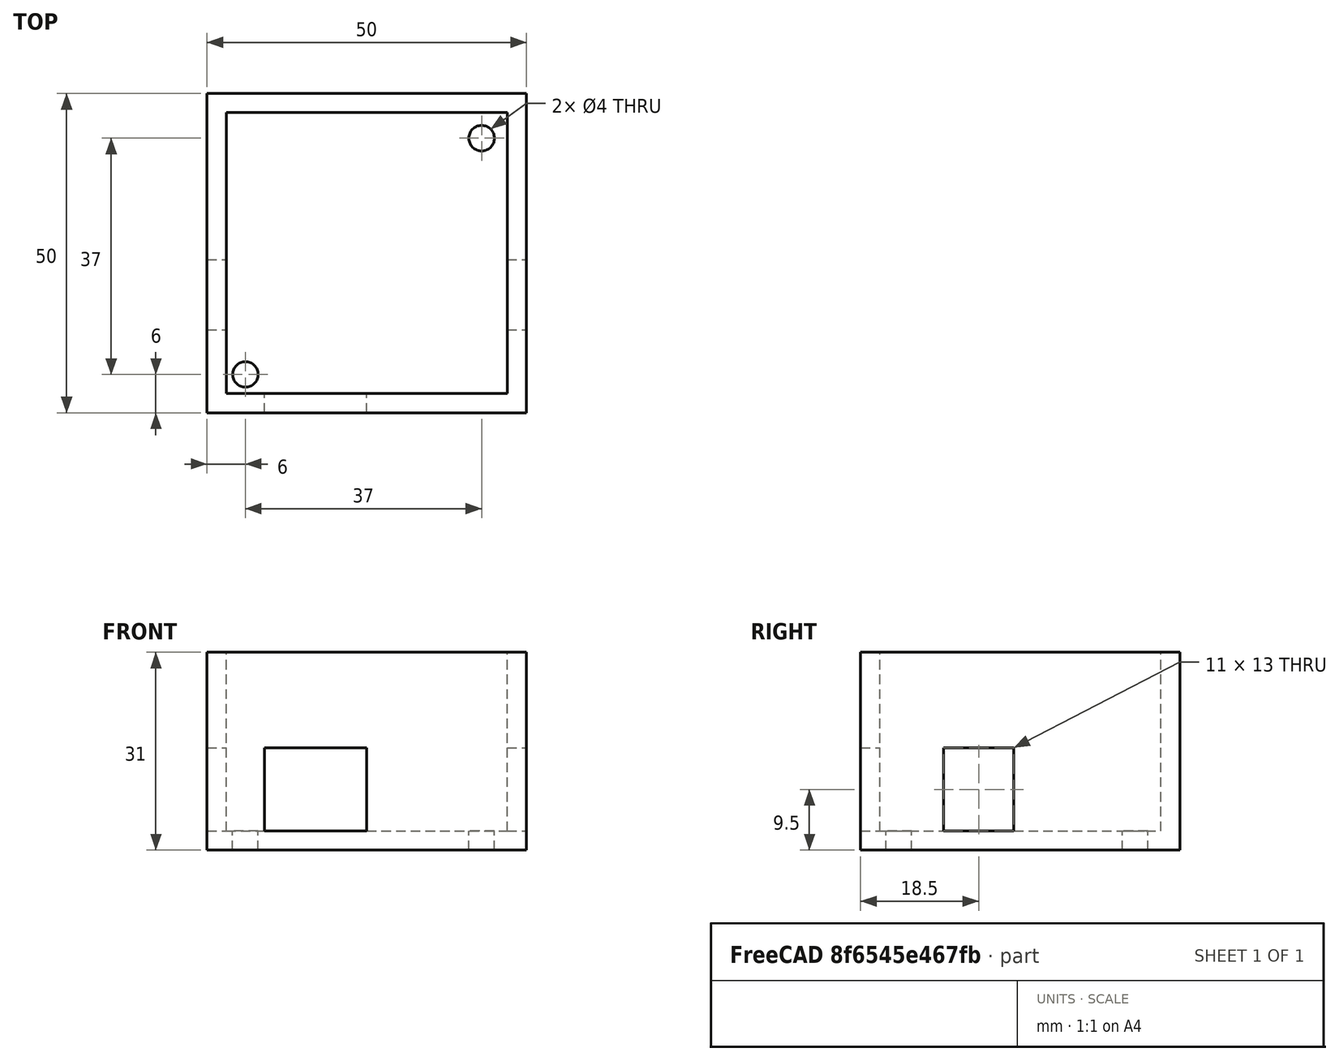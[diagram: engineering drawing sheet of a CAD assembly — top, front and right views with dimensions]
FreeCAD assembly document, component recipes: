
FREECAD ASSEMBLY — COMPONENT RECIPES ("caja_controlador_ruedas")

This assembly document has 2 components, labeled P0..P1 below (a component is one placed body or linked part). 0 of them carry a construction recipe — the FreeCAD feature program that regenerates the part from scratch, quoted from this document or its linked companion documents; the rest are supplied as boundary geometry only. No exploded tour is included for this assembly.
COMPONENT P0 — geometry summary ("Cube004"; no construction recipe available for this part):
  bounding box: 13.0 x 11.0 x 10.0 mm
  tessellated surface: 12 triangles
  volume: 1430 mm^3 (100% of its bounding box)
  symmetry: 2-fold rotationally symmetric about the x axis; 2-fold rotationally symmetric about the y axis; 2-fold rotationally symmetric about the z axis; mirror-symmetric across its x mid-plane, y mid-plane, z mid-plane
COMPONENT P1 — geometry summary ("Cylinder001"; no construction recipe available for this part):
  bounding box: 10.0 x 4.0 x 4.0 mm
  tessellated surface: 500 triangles
  volume: 126 mm^3 (79% of its bounding box)
  symmetry: 2-fold rotationally symmetric about the x axis; 2-fold rotationally symmetric about the y axis; revolution-symmetric about the z axis through its bounding-box center; mirror-symmetric across its x mid-plane, y mid-plane, z mid-plane
PROVENANCE & LICENSES
A FreeCAD (.FCStd) document from a public repository crawl; recipes are the document's own serialized feature recipes (and, for linked parts, companion documents' recipes).
License: lgpl-2.1.
